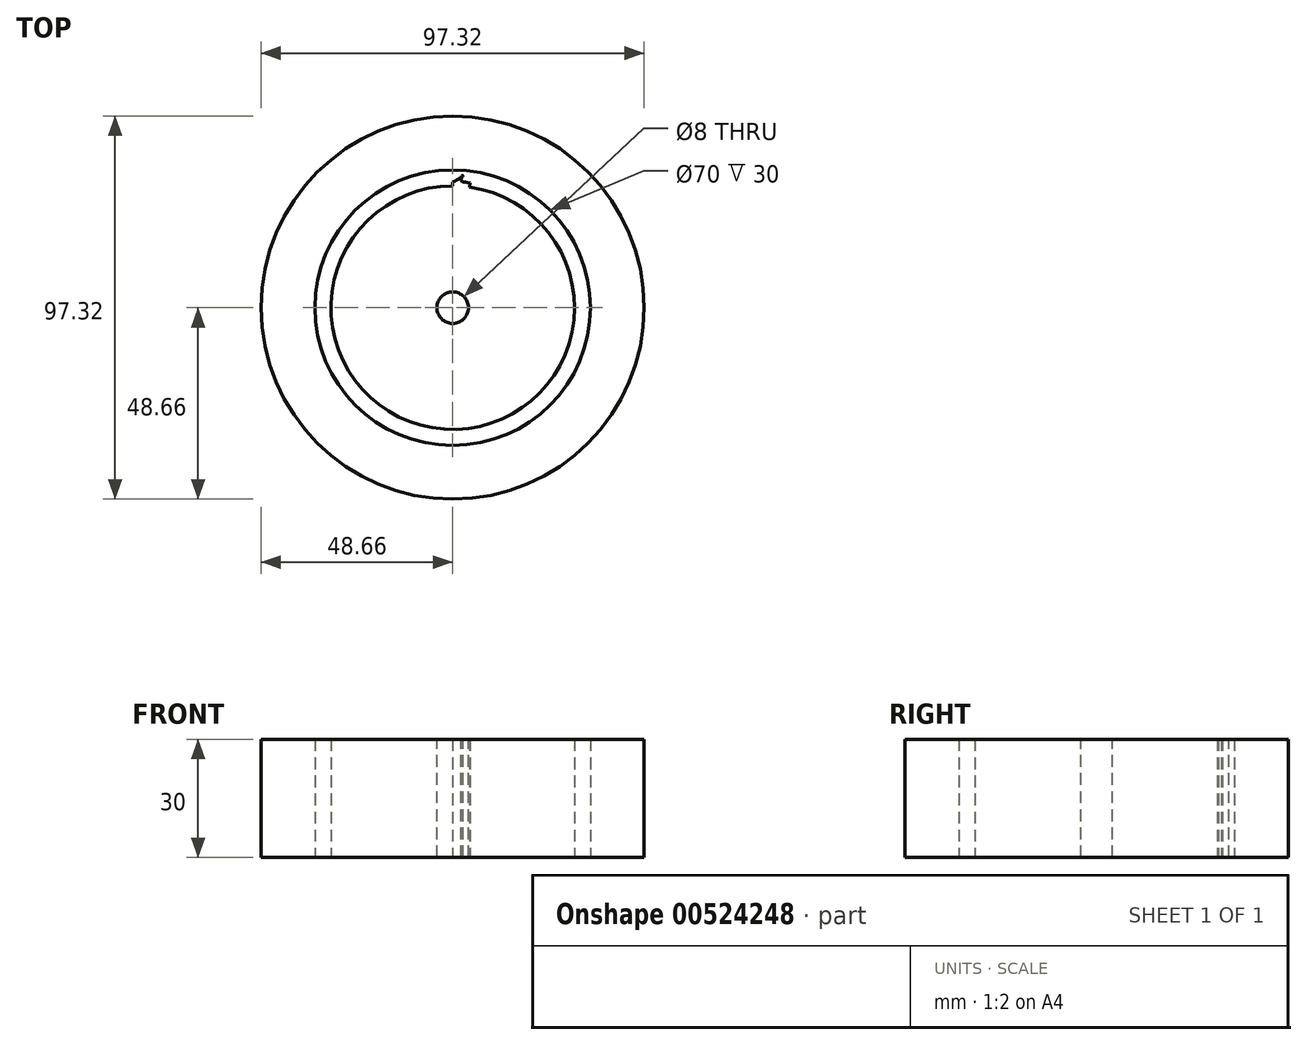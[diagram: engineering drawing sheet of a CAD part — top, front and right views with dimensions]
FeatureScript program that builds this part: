
annotation { "Feature Type Name" : "Feature", "Feature Type Description" : "" }
export const myFeature = defineFeature(function(context is Context, id is Id, definition is map)
    precondition{}
    {
        {
            var Q0;
            Q0=qCreatedBy(makeId("Top.planeOp"),FACE);
            var sketch = newSketch(context, id + "F0", { "sketchPlane" : qUnion([Q0])});
            skCircle(sketch, "E0", {"center": v(0, 0) * mm, "radius": 48.66 * mm});
            skSolve(sketch);
        }
        {
            var Q0;
            Q0=qCreatedBy(makeId("Top.planeOp"),FACE);
            var sketch = newSketch(context, id + "F1", { "sketchPlane" : qUnion([Q0])});
            skCircle(sketch, "E1", {"center": v(0, 0) * mm, "radius": 35 * mm});
            skSolve(sketch);
        }
        {
            var Q0;
            Q0=qCreatedBy(makeId("Top.planeOp"),FACE);
            var sketch = newSketch(context, id + "F2", { "sketchPlane" : qUnion([Q0])});
            skCircle(sketch, "E2", {"center": v(0, 0) * mm, "radius": 30.93 * mm});
            skSolve(sketch);
        }
        {
            var Q0;
            Q0=qCreatedBy(makeId("Top.planeOp"),FACE);
            var sketch = newSketch(context, id + "F3", { "sketchPlane" : qUnion([Q0])});
            skCircle(sketch, "E3", {"center": v(0, 0) * mm, "radius": 4 * mm});
            skSolve(sketch);
        }
        {
            var Q0;
            Q0=qCreatedBy(makeId("Top.planeOp"),FACE);
            var sketch = newSketch(context, id + "F4", { "sketchPlane" : qUnion([Q0])});
            skCircle(sketch, "E4", {"center": v(0, 0) * mm, "radius": 31.97 * mm, "construction": true});
            skLineSegment(sketch, "E5", {"start": v(4.38, 31.67) * mm, "end": v(0, 0) * mm, "construction": true});
            skLineSegment(sketch, "E6", {"start": v(4.38, 31.67) * mm, "end": v(3.44, 24.85) * mm});
            skLineSegment(sketch, "E7", {"start": v(3.44, 24.85) * mm, "end": v(0, 24.85) * mm});
            skLineSegment(sketch, "E8", {"start": v(0, 24.85) * mm, "end": v(0, 31.97) * mm});
            skFitSpline(sketch, "E9", {"points": [v(0, 31.97) * mm, v(2.6, 33.58) * mm, v(2.12, 32.58) * mm, v(4.38, 31.67) * mm], "startDerivative": vector(13.13, 5.44) * mm, "endDerivative": vector(16.32, -2.86) * mm});
            skSolve(sketch);
        }
        {
            var Q0;
            Q0=qSketchRegion(id+"F0",true);
            extrude(context, id + "F5", {"entities" : qUnion([Q0]), "endBound" : BoundingType.SYMMETRIC, "depth" : 30 * mm, "offsetDistance" : 25 * mm});
        }
        {
            var Q0;
            Q0=qSketchRegion(id+"F1",true);
            extrude(context, id + "F6", {"entities" : qUnion([Q0]), "operationType" : NewBodyOperationType.REMOVE, "endBound" : BoundingType.THROUGH_ALL, "depth" : 30 * mm, "hasSecondDirection" : true, "secondDirectionBound" : SecondDirectionBoundingType.THROUGH_ALL, "secondDirectionOppositeDirection" : true, "secondDirectionDepth" : 25 * mm});
        }
        {
            var Q0;
            Q0=qSketchRegion(id+"F2",true);
            extrude(context, id + "F7", {"entities" : qUnion([Q0]), "endBound" : BoundingType.SYMMETRIC, "depth" : 30 * mm, "offsetDistance" : 25 * mm});
        }
        {
            var Q0;
            Q0=qSketchRegion(id+"F3",true);
            extrude(context, id + "F8", {"entities" : qUnion([Q0]), "operationType" : NewBodyOperationType.REMOVE, "endBound" : BoundingType.THROUGH_ALL, "oppositeDirection" : true, "depth" : 25 * mm, "hasSecondDirection" : true, "secondDirectionBound" : SecondDirectionBoundingType.THROUGH_ALL, "secondDirectionOppositeDirection" : false, "secondDirectionDepth" : 25 * mm});
        }
        {
            var Q0;
            Q0=qSketchRegion(id+"F4",true);
            extrude(context, id + "F9", {"entities" : qUnion([Q0]), "operationType" : NewBodyOperationType.ADD, "endBound" : BoundingType.SYMMETRIC, "depth" : 30 * mm, "offsetDistance" : 25 * mm});
        }
    });
